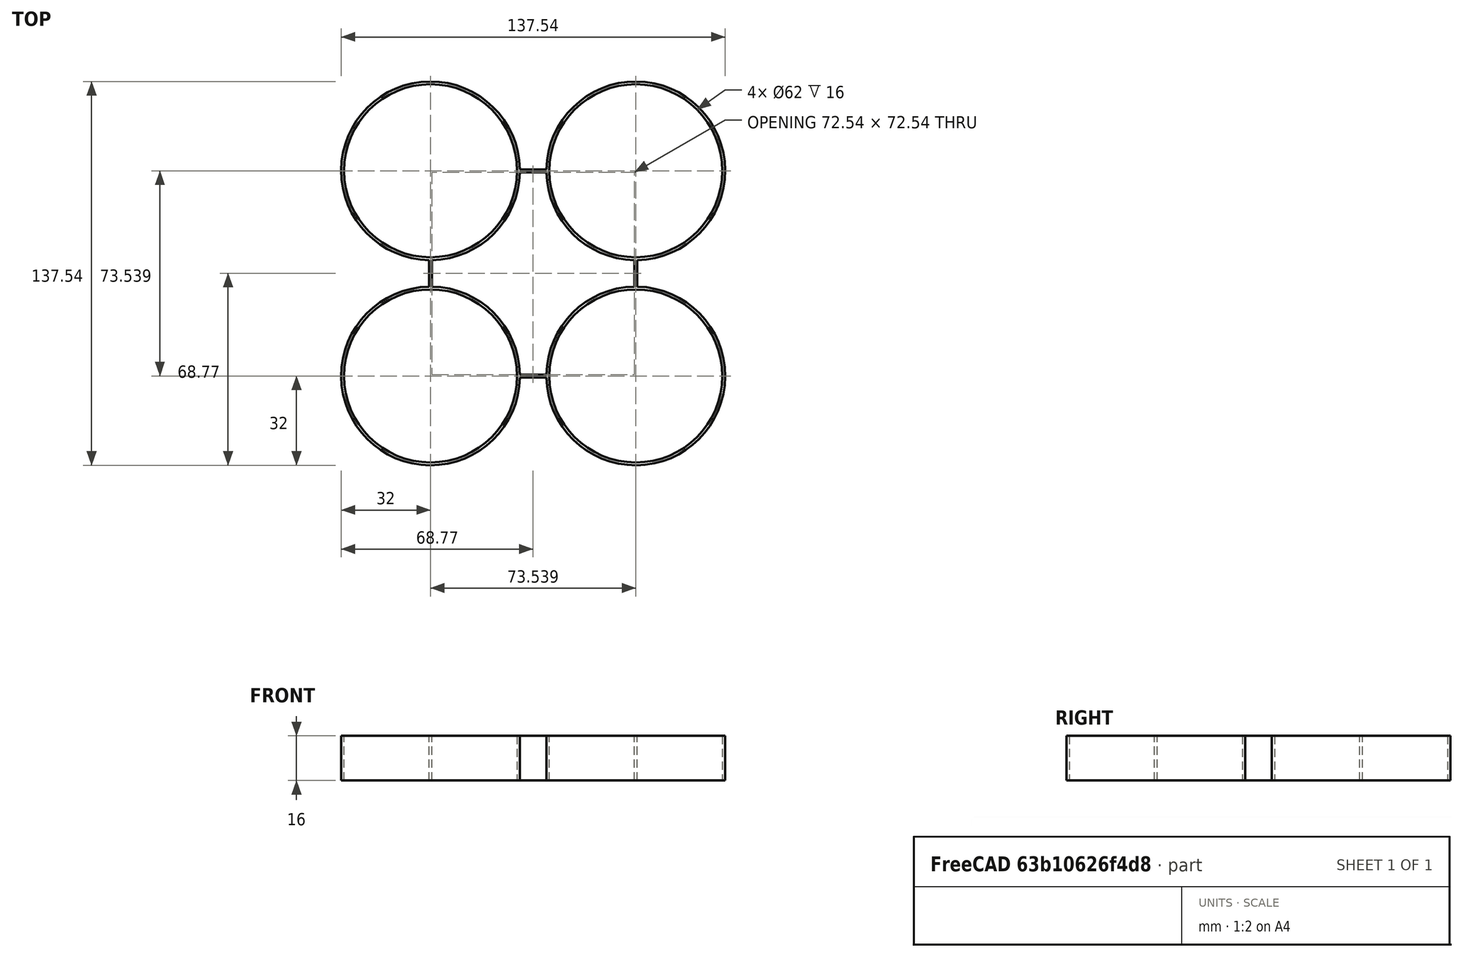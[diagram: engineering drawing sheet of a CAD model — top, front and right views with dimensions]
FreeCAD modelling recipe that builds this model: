
FCSTD DOCUMENT  (FreeCAD 0.19R23578 (Git))
Label: shroud
License: All rights reserved
LicenseURL: http://en.wikipedia.org/wiki/All_rights_reserved
objects: Part::Feature×6, Part::Extrusion×6, Part::Cut×5
note: 17 computed .brp shape members not serialized (recipe doc carries the construction recipe); baked Part::Feature solids carry a one-line shape summary decoded from their .brp

FEATURE [Part::Feature] Shape
  shape: bbox 62 x 62 x 2e-07 mm, 0 faces, 0 solids (baked)
FEATURE [Part::Feature] Shape001
  shape: bbox 62 x 62 x 2e-07 mm, 0 faces, 0 solids (baked)
FEATURE [Part::Feature] Shape002
  shape: bbox 62 x 62 x 2e-07 mm, 0 faces, 0 solids (baked)
FEATURE [Part::Feature] Shape003
  shape: bbox 62 x 62 x 2e-07 mm, 0 faces, 0 solids (baked)
FEATURE [Part::Feature] Face
  shape: bbox 72.54 x 72.54 x 2e-07 mm, 1 faces, 0 solids (baked)
FEATURE [Part::Feature] Face001
  shape: bbox 137.5 x 137.5 x 2e-07 mm, 1 faces, 0 solids (baked)
FEATURE [Part::Extrusion] Extrude
  Base = -> Face001
  Dir = (0,0,1)
  DirMode = 0
  FaceMakerClass = Part::FaceMakerBullseye
  LengthFwd = 16
  LengthRev = 0
  Solid = false
  Symmetric = false
FEATURE [Part::Extrusion] Extrude001
  Base = -> Shape
  Dir = (0,0,1)
  DirMode = 0
  FaceMakerClass = Part::FaceMakerBullseye
  LengthFwd = 20
  LengthRev = 0
  Solid = true
  Symmetric = false
FEATURE [Part::Extrusion] Extrude002
  Base = -> Shape001
  Dir = (0,0,1)
  DirMode = 0
  FaceMakerClass = Part::FaceMakerBullseye
  LengthFwd = 20
  LengthRev = 0
  Solid = true
  Symmetric = false
FEATURE [Part::Extrusion] Extrude003
  Base = -> Shape002
  Dir = (0,0,1)
  DirMode = 0
  FaceMakerClass = Part::FaceMakerBullseye
  LengthFwd = 20
  LengthRev = 0
  Solid = true
  Symmetric = false
FEATURE [Part::Extrusion] Extrude004
  Base = -> Shape003
  Dir = (0,0,1)
  DirMode = 0
  FaceMakerClass = Part::FaceMakerBullseye
  LengthFwd = 20
  LengthRev = 0
  Solid = true
  Symmetric = false
FEATURE [Part::Extrusion] Extrude005
  Base = -> Face
  Dir = (0,0,1)
  DirMode = 0
  FaceMakerClass = Part::FaceMakerBullseye
  LengthFwd = 20
  LengthRev = 0
  Solid = true
  Symmetric = false
FEATURE [Part::Cut] Cut
  Base = -> Extrude
  Tool = -> Extrude001
FEATURE [Part::Cut] Cut001
  Base = -> Cut
  Tool = -> Extrude005
FEATURE [Part::Cut] Cut002
  Base = -> Cut001
  Tool = -> Extrude004
FEATURE [Part::Cut] Cut003
  Base = -> Cut002
  Tool = -> Extrude003
FEATURE [Part::Cut] Cut004
  Base = -> Cut003
  Tool = -> Extrude002
